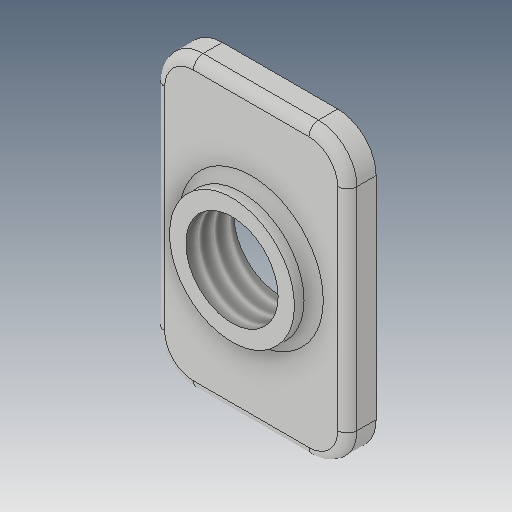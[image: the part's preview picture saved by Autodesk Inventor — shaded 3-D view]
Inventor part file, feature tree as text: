
AUTODESK INVENTOR PART (.ipt)
format: ipt  version: 2017 (Build 210142000, 142)  size: 178,176 bytes
history: native  units: mm
features: other x3, sketch x2
ambient origin geometry x8: Origin, YZ Plane, XZ Plane, XY Plane, X Axis, Y Axis, Z Axis, Center Point
bodies: Solid1 (feature_tree)
feature tree (5):
  other  "M5 Tee Nut-Generic_MIR_CPY.ipt"
  other  "Solid1::M5 Tee Nut-Generic_MIR_CPY.ipt"
  other  "TaggingFeature1"
  sketch  "Sketch1"  dims[d0=10.0mm]
  sketch  "Sketch2"
